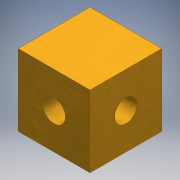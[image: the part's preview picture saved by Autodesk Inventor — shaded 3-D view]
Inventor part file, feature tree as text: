
AUTODESK INVENTOR PART (.ipt)
format: ipt  version: 2020.2 (Build 242310000, 310)  size: 120,832 bytes
history: native  units: mm
features: other x3, sketch x3, hole x2, extrude x1
ambient origin geometry x8: Origin, YZ Plane, XZ Plane, XY Plane, X Axis, Y Axis, Z Axis, Center Point
bodies: Body1 (feature_tree)
feature tree (9):
  other  "ソリッド1"
  extrude  "押し出し1"  Depth=8.0mm
  hole  "穴1"  [1 undecoded]
  hole  "穴2"  [1 undecoded]
  sketch  "スケッチ1"
  sketch  "スケッチ2"
  sketch  "スケッチ3"
  other  "断面エッジを投影1"
  other  "断面エッジを投影2"
note: 2 required parameter values undecoded (feature->parameter linkage not recoverable at this tier; creation-order binding heuristic only, values carry confidence <= 0.55)
